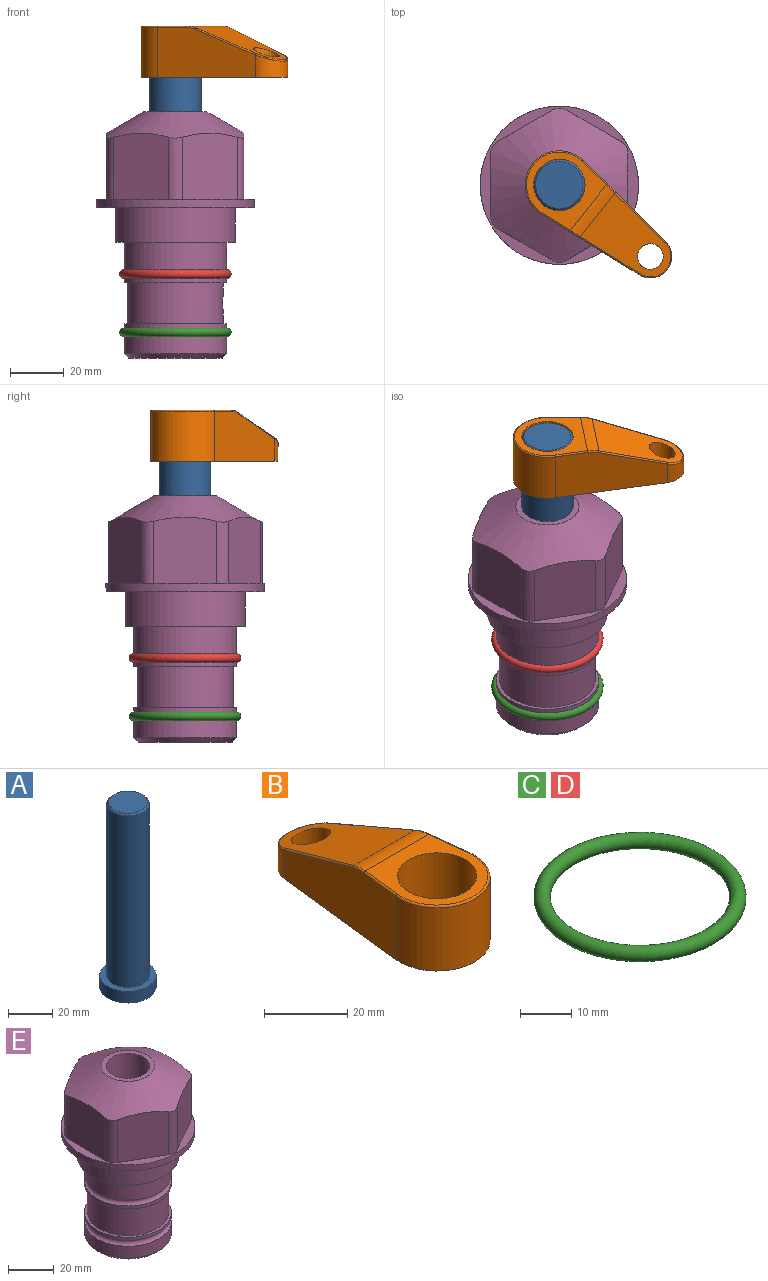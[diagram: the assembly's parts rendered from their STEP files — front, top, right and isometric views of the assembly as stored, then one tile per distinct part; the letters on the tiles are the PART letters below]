
ASSEMBLY  parts=5 mates=3
PART A: 6 faces, bbox 25.4x25.4x101.6 mm
  f0: plane 17.46x17.46mm, normal (0,0,1), area 239.5mm2, adj f5
  f1: plane 25.4x25.4mm, normal (0,0,-1), area 506.7mm2, adj f2
  f2: cylinder r=12.7mm len=25.4mm, axis (0,0,1), area 506.7mm2, adj f1,f3
  f3: plane 25.4x25.4mm, normal (0,0,1), area 221.7mm2, adj f2,f4
  f4: cylinder r=9.53mm len=94.46mm, axis (0,0,1), area 5653mm2, adj f3,f5
  f5: cone r=8.73mm half-angle=45deg, axis (0,0,-1), area 64.4mm2, adj f0,f4
PART B: 44 faces, bbox 27.5x64.5x19.1 mm
  f0: plane 2.3x0.95mm, normal (0,0,-1), area 1mm2, adj f25,f30,f34
  f1: plane 63.5x25.4mm, normal (0,0,-1), area 561.7mm2, adj f2,f3,f4,f5,f6,f7,f19,f20
  f2: cylinder r=12.7mm len=25.4mm, axis (0,0,-1), area 792.2mm2, adj f1,f3,f5,f13
  f3: plane 42.33x18.54mm, normal (0.99,0.11,0), area 647mm2, adj f1,f2,f4,f11,f12,f14
  f4: cylinder r=7.94mm len=15.78mm, axis (0,0,-1), area 158.6mm2, adj f1,f3,f5,f16
  f5: plane 42.33x18.54mm, normal (-0.99,0.11,0), area 647mm2, adj f1,f2,f4,f15,f17,f18
  f6: cylinder r=9.53mm len=19.05mm, axis (0,0,-1), area 1140.1mm2, adj f1,f8
  f7: cylinder r=4.76mm len=10.98mm, axis (0,0,-1), area 276.1mm2, adj f1,f9
  f8: plane 25.83x24.38mm, normal (0,0,1), area 262.2mm2, adj f6,f10,f11,f13,f15
  f9: plane 32.49x20.55mm, normal (0,0.34,0.94), area 489.9mm2, adj f7,f10,f14,f16,f18
  f10: cylinder r=12.7mm len=21.49mm, axis (-1,0,0), area 93.2mm2, adj f8,f9,f12,f17
  f11: cylinder r=0.51mm len=12.34mm, axis (0.11,-0.99,0), area 9.9mm2, adj f3,f8,f12,f13
  f12: bspline ~7.62x1.64mm, area 3.5mm2, adj f3,f10,f11,f14
  f13: torus R=12.19mm, axis (0,0,1), area 33.6mm2, adj f2,f8,f11,f15
  f14: cylinder r=0.51mm len=26.01mm, axis (0.1,-0.93,0.34), area 21.6mm2, adj f3,f9,f12,f16
  f15: cylinder r=0.51mm len=12.34mm, axis (0.11,0.99,0), area 9.9mm2, adj f5,f8,f13,f17
  f16: bspline ~15.78x7.05mm, area 15.7mm2, adj f4,f9,f14,f18
  f17: bspline ~7.62x1.64mm, area 3.5mm2, adj f5,f10,f15,f18
  f18: cylinder r=0.51mm len=26.01mm, axis (0.1,0.93,-0.34), area 21.6mm2, adj f5,f9,f16,f17
  f19: plane 21.6x14.29mm, normal (-0.99,-0.11,0), area 242.6mm2, adj f1,f26,f28,f34,f36,f38
  f20: plane 21.6x14.29mm, normal (0.99,-0.11,0), area 242.6mm2, adj f1,f27,f29,f37,f39,f41
  f21: cylinder r=12.7mm len=14.29mm, axis (0,0,-1), area 173.2mm2, adj f1,f26,f27,f30,f31,f33
  f22: cylinder r=7.94mm len=7.63mm, axis (0,0,-1), area 53.8mm2, adj f1,f28,f29,f42
  f23: plane 2.3x0.95mm, normal (0,0,-1), area 1mm2, adj f25,f33,f37
  f24: plane 17.94x12.32mm, normal (0,-0.34,-0.94), area 191.2mm2, adj f25,f38,f41,f42
  f25: cylinder r=9.53mm len=12.93mm, axis (-1,0,0), area 37.5mm2, adj f0,f23,f24,f31,f36,f39
  f26: cylinder r=1.59mm len=14.29mm, axis (0,0,-1), area 49mm2, adj f1,f19,f21,f32
  f27: cylinder r=1.59mm len=14.29mm, axis (0,0,-1), area 49mm2, adj f1,f20,f21,f35
  f28: cylinder r=1.59mm len=7.28mm, axis (0,0,-1), area 22.1mm2, adj f1,f19,f22,f40
  f29: cylinder r=1.59mm len=7.28mm, axis (0,0,-1), area 22.1mm2, adj f1,f20,f22,f43
  f30: torus R=14.29mm, axis (0,0,1), area 5.8mm2, adj f0,f21,f31,f32
  f31: bspline ~11.06x2.73mm, area 20.8mm2, adj f21,f25,f30,f33
  f32: sphere r=1.59mm, area 5.4mm2, adj f26,f30,f34
  f33: torus R=14.29mm, axis (0,0,1), area 5.8mm2, adj f21,f23,f31,f35
  f34: cylinder r=1.59mm len=1.68mm, axis (-0.11,0.99,0), area 2.4mm2, adj f0,f19,f32,f36
  f35: sphere r=1.59mm, area 5.4mm2, adj f27,f33,f37
  f36: bspline ~5.82x2.33mm, area 7.7mm2, adj f19,f25,f34,f38
  f37: cylinder r=1.59mm len=1.68mm, axis (0.11,0.99,0), area 2.4mm2, adj f20,f23,f35,f39
  f38: cylinder r=1.59mm len=18.33mm, axis (0.1,-0.93,0.34), area 46.7mm2, adj f19,f24,f36,f40
  f39: bspline ~5.82x2.33mm, area 7.7mm2, adj f20,f25,f37,f41
  f40: sphere r=1.59mm, area 3.6mm2, adj f28,f38,f42
  f41: cylinder r=1.59mm len=18.33mm, axis (0.1,0.93,-0.34), area 46.7mm2, adj f20,f24,f39,f43
  f42: bspline ~8.31x1.84mm, area 15.3mm2, adj f22,f24,f40,f43
  f43: sphere r=1.59mm, area 3.6mm2, adj f29,f41,f42
PART C: 1 faces, bbox 44.7x44.7x3.2 mm
  f0: torus R=19.05mm, axis (0,0,1), area 1193.9mm2
PART D: same geometry as C
PART E: 36 faces, bbox 58.7x58.7x91.2 mm
  f0: cylinder r=17.78mm len=35.56mm, axis (0,0,1), area 1670.8mm2, adj f23,f24,f31
  f1: cylinder r=19.05mm len=38.1mm, axis (0,0,1), area 1191.9mm2, adj f26,f27,f30
  f2: plane 58.66x58.66mm, normal (0,0,-1), area 1150.6mm2, adj f3,f28
  f3: cylinder r=29.33mm len=58.66mm, axis (0,0,-1), area 585.1mm2, adj f2,f4
  f4: plane 58.66x58.66mm, normal (0,0,1), area 475.9mm2, adj f3,f5,f6,f7,f8,f9,f10,f11
  f5: plane 24.5x20.32mm, normal (-0.5,0.87,0), area 562.8mm2, adj f4,f15,f16,f17
  f6: plane 24.5x20.32mm, normal (0.5,0.87,0), area 562.8mm2, adj f4,f14,f15,f17
  f7: plane 24.5x23.48mm, normal (1,0,0), area 562.8mm2, adj f4,f13,f14,f17
  f8: plane 24.5x20.32mm, normal (0.5,-0.87,0), area 562.8mm2, adj f4,f12,f13,f17
  f9: plane 24.5x20.32mm, normal (-0.5,-0.87,0), area 562.8mm2, adj f4,f11,f12,f17
  f10: plane 24.5x23.48mm, normal (-1,0,0), area 562.8mm2, adj f4,f11,f16,f17
  f11: cylinder r=5.08mm len=23.01mm, axis (0,0,-1), area 121.2mm2, adj f4,f9,f10,f17
  f12: cylinder r=5.08mm len=23.01mm, axis (0,0,-1), area 121.2mm2, adj f4,f8,f9,f17
  f13: cylinder r=5.08mm len=23.01mm, axis (0,0,-1), area 121.2mm2, adj f4,f7,f8,f17
  f14: cylinder r=5.08mm len=23.01mm, axis (0,0,-1), area 121.2mm2, adj f4,f6,f7,f17
  f15: cylinder r=5.08mm len=23.01mm, axis (0,0,-1), area 121.2mm2, adj f4,f5,f6,f17
  f16: cylinder r=5.08mm len=23.01mm, axis (0,0,-1), area 121.2mm2, adj f4,f5,f10,f17
  f17: cone r=11.73mm half-angle=60deg, axis (0,0,-1), area 2071.8mm2, adj f5,f6,f7,f8,f9,f10,f11,f12
  f18: plane 23.46x23.46mm, normal (0,0,1), area 147.4mm2, adj f17,f35
  f19: plane 34.93x34.93mm, normal (0,0,-1), area 958mm2, adj f29
  f20: cylinder r=19.05mm len=38.1mm, axis (0,0,1), area 760.1mm2, adj f21,f29
  f21: torus R=19.05mm, axis (0,0,1), area 565.3mm2, adj f20,f22
  f22: cylinder r=19.05mm len=38.1mm, axis (0,0,1), area 190mm2, adj f21,f23
  f23: plane 38.1x38.1mm, normal (0,0,1), area 146.9mm2, adj f0,f22
  f24: plane 38.1x38.1mm, normal (0,0,-1), area 146.9mm2, adj f0,f25
  f25: cylinder r=19.05mm len=38.1mm, axis (0,0,1), area 190mm2, adj f24,f26
  f26: torus R=19.05mm, axis (0,0,1), area 565.3mm2, adj f1,f25
  f27: plane 44.45x44.45mm, normal (0,0,-1), area 411.7mm2, adj f1,f28
  f28: cylinder r=22.23mm len=44.45mm, axis (0,0,1), area 1773.5mm2, adj f2,f27
  f29: cone r=19.05mm half-angle=45deg, axis (0,0,1), area 257.5mm2, adj f19,f20
  f30: cylinder r=3.17mm len=6.75mm, axis (-1,0,0), area 128mm2, adj f1,f33
  f31: cylinder r=3.17mm len=6.35mm, axis (-1,0,0), area 102.5mm2, adj f0,f33
  f32: plane 25.4x25.4mm, normal (0,0,1), area 506.7mm2, adj f33
  f33: cylinder r=12.7mm len=66.42mm, axis (0,0,-1), area 5236.2mm2, adj f30,f31,f32,f34
  f34: cone r=9.53mm half-angle=30deg, axis (0,0,-1), area 443.4mm2, adj f33,f35
  f35: cylinder r=9.53mm len=19.05mm, axis (0,0,-1), area 849mm2, adj f18,f34
PLACE A rot(axis=(0,0,-1),38.1deg) t=(0,0,-6.27)mm
PLACE B rot(axis=(0,0,-1),128.1deg) t=(0,0,48.34)mm
PLACE C t=(0,0,-21.59)mm
PLACE D at identity
PLACE E at identity fixed
MATE fastened C.f0 <-> E.f0  axis (0,0,1) through (0,0,-46.1)mm
MATE cylindrical A.f2 <-> E.f0  axis (0,0,1) through (0,0,19.37)mm
MATE fastened B.f2 <-> A.f2  axis (0,0,1) through (0,0,67.39)mm
